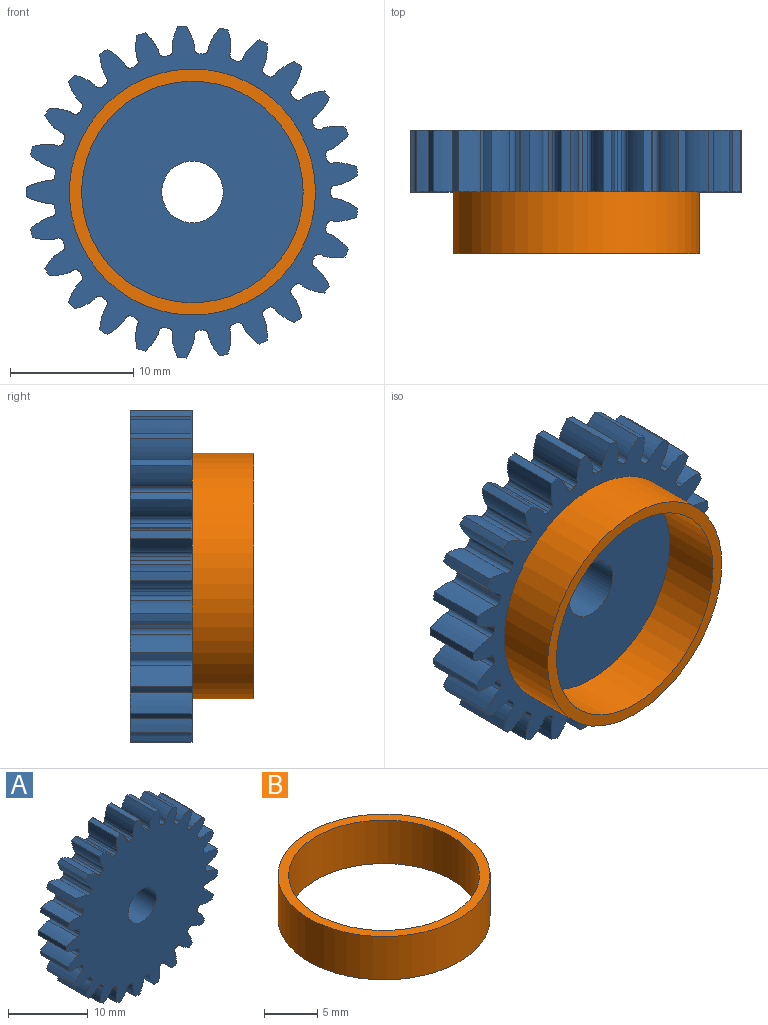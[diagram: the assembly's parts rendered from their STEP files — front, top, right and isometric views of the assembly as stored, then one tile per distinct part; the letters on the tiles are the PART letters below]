
ASSEMBLY  parts=2 mates=1
PART A: 153 faces, bbox 26.9x5x27 mm
  f0: cylinder r=13.5mm len=5mm, axis (0,1,0), area 3.6mm2, adj f24,f27,f138,f150
  f1: cylinder r=13.5mm len=5mm, axis (0,1,0), area 3.6mm2, adj f24,f27,f145,f148
  f2: cylinder r=13.5mm len=5mm, axis (0,1,0), area 3.6mm2, adj f24,f27,f133,f140
  f3: cylinder r=13.5mm len=5mm, axis (0,1,0), area 3.6mm2, adj f24,f27,f128,f135
  f4: cylinder r=13.5mm len=5mm, axis (0,1,0), area 3.6mm2, adj f24,f27,f123,f130
  f5: cylinder r=13.5mm len=5mm, axis (0,1,0), area 3.6mm2, adj f24,f27,f113,f125
  f6: cylinder r=13.5mm len=5mm, axis (0,1,0), area 3.6mm2, adj f24,f27,f108,f120
  f7: cylinder r=13.5mm len=5mm, axis (0,1,0), area 3.6mm2, adj f24,f27,f115,f118
  f8: cylinder r=13.5mm len=5mm, axis (0,1,0), area 3.6mm2, adj f24,f27,f103,f110
  f9: cylinder r=13.5mm len=5mm, axis (0,1,0), area 3.6mm2, adj f24,f27,f98,f105
  f10: cylinder r=13.5mm len=5mm, axis (0,1,0), area 3.6mm2, adj f24,f27,f93,f100
  f11: cylinder r=13.5mm len=5mm, axis (0,1,0), area 3.6mm2, adj f24,f27,f78,f95
  f12: cylinder r=13.5mm len=5mm, axis (0,1,0), area 3.6mm2, adj f24,f27,f28,f90
  f13: cylinder r=13.5mm len=5mm, axis (0,1,0), area 3.6mm2, adj f24,f27,f85,f88
  f14: cylinder r=13.5mm len=5mm, axis (0,1,0), area 3.6mm2, adj f24,f27,f73,f80
  f15: cylinder r=13.5mm len=5mm, axis (0,1,0), area 3.6mm2, adj f24,f27,f75,f83
  f16: cylinder r=13.5mm len=5mm, axis (0,1,0), area 3.6mm2, adj f24,f27,f70,f143
  f17: cylinder r=13.5mm len=5mm, axis (0,1,0), area 3.6mm2, adj f24,f27,f65,f68
  f18: cylinder r=13.5mm len=5mm, axis (0,1,0), area 3.6mm2, adj f24,f27,f60,f63
  f19: cylinder r=13.5mm len=5mm, axis (0,1,0), area 3.6mm2, adj f24,f27,f55,f58
  f20: cylinder r=13.5mm len=5mm, axis (0,1,0), area 3.6mm2, adj f24,f27,f43,f50
  f21: cylinder r=13.5mm len=5mm, axis (0,1,0), area 3.6mm2, adj f24,f27,f33,f45
  f22: cylinder r=13.5mm len=5mm, axis (0,1,0), area 3.6mm2, adj f24,f27,f40,f53
  f23: cylinder r=13.5mm len=5mm, axis (0,1,0), area 3.6mm2, adj f24,f27,f35,f38
  f24: plane 26.99x26.94mm, normal (0,-1,0), area 464mm2, adj f0,f1,f2,f3,f4,f5,f6,f7
  f25: cylinder r=2.5mm len=5mm, axis (0,1,0), area 78.5mm2, adj f24,f27
  f26: cylinder r=13.5mm len=5mm, axis (0,1,0), area 3.6mm2, adj f24,f27,f30,f48
  f27: plane 26.99x26.94mm, normal (0,1,0), area 464mm2, adj f0,f1,f2,f3,f4,f5,f6,f7
  f28: extruded ~5x1.83mm, area 10mm2, adj f12,f24,f27,f31
  f29: cylinder r=11.25mm len=5mm, axis (0,1,0), area 1.7mm2, adj f24,f27,f31,f32
  f30: extruded ~5x1.83mm, area 10mm2, adj f24,f26,f27,f32
  f31: cylinder r=0.38mm len=5mm, axis (0,1,0), area 2.9mm2, adj f24,f27,f28,f29
  f32: cylinder r=0.38mm len=5mm, axis (0,1,0), area 2.9mm2, adj f24,f27,f29,f30
  f33: extruded ~5x1.86mm, area 10mm2, adj f21,f24,f27,f36
  f34: cylinder r=11.25mm len=5mm, axis (0,1,0), area 1.7mm2, adj f24,f27,f36,f37
  f35: extruded ~5x1.82mm, area 10mm2, adj f23,f24,f27,f37
  f36: cylinder r=0.38mm len=5mm, axis (0,1,0), area 2.9mm2, adj f24,f27,f33,f34
  f37: cylinder r=0.38mm len=5mm, axis (0,1,0), area 2.9mm2, adj f24,f27,f34,f35
  f38: extruded ~5x1.64mm, area 10mm2, adj f23,f24,f27,f41
  f39: cylinder r=11.25mm len=5mm, axis (0,1,0), area 1.7mm2, adj f24,f27,f41,f42
  f40: extruded ~5x1.96mm, area 10mm2, adj f22,f24,f27,f42
  f41: cylinder r=0.38mm len=5mm, axis (0,1,0), area 2.9mm2, adj f24,f27,f38,f39
  f42: cylinder r=0.38mm len=5mm, axis (0,1,0), area 2.9mm2, adj f24,f27,f39,f40
  f43: extruded ~5x1.98mm, area 10mm2, adj f20,f24,f27,f46
  f44: cylinder r=11.25mm len=5mm, axis (0,1,0), area 1.7mm2, adj f24,f27,f46,f47
  f45: extruded ~5x1.56mm, area 10mm2, adj f21,f24,f27,f47
  f46: cylinder r=0.38mm len=5mm, axis (0,1,0), area 2.9mm2, adj f24,f27,f43,f44
  f47: cylinder r=0.38mm len=5mm, axis (0,1,0), area 2.9mm2, adj f24,f27,f44,f45
  f48: extruded ~5x1.96mm, area 10mm2, adj f24,f26,f27,f51
  f49: cylinder r=11.25mm len=5mm, axis (0,1,0), area 1.7mm2, adj f24,f27,f51,f52
  f50: extruded ~5x1.57mm, area 10mm2, adj f20,f24,f27,f52
  f51: cylinder r=0.38mm len=5mm, axis (0,1,0), area 2.9mm2, adj f24,f27,f48,f49
  f52: cylinder r=0.38mm len=5mm, axis (0,1,0), area 2.9mm2, adj f24,f27,f49,f50
  f53: extruded ~5x1.5mm, area 10mm2, adj f22,f24,f27,f56
  f54: cylinder r=11.25mm len=5mm, axis (0,1,0), area 1.7mm2, adj f24,f27,f56,f57
  f55: extruded ~5x1.98mm, area 10mm2, adj f19,f24,f27,f57
  f56: cylinder r=0.38mm len=5mm, axis (0,1,0), area 2.9mm2, adj f24,f27,f53,f54
  f57: cylinder r=0.38mm len=5mm, axis (0,1,0), area 2.9mm2, adj f24,f27,f54,f55
  f58: extruded ~5x1.77mm, area 10mm2, adj f19,f24,f27,f61
  f59: cylinder r=11.25mm len=5mm, axis (0,1,0), area 1.7mm2, adj f24,f27,f61,f62
  f60: extruded ~5x1.87mm, area 10mm2, adj f18,f24,f27,f62
  f61: cylinder r=0.38mm len=5mm, axis (0,1,0), area 2.9mm2, adj f24,f27,f58,f59
  f62: cylinder r=0.38mm len=5mm, axis (0,1,0), area 2.9mm2, adj f24,f27,f59,f60
  f63: extruded ~5x1.94mm, area 10mm2, adj f18,f24,f27,f66
  f64: cylinder r=11.25mm len=5mm, axis (0,1,0), area 1.7mm2, adj f24,f27,f66,f67
  f65: extruded ~5x1.65mm, area 10mm2, adj f17,f24,f27,f67
  f66: cylinder r=0.38mm len=5mm, axis (0,1,0), area 2.9mm2, adj f24,f27,f63,f64
  f67: cylinder r=0.38mm len=5mm, axis (0,1,0), area 2.9mm2, adj f24,f27,f64,f65
  f68: extruded ~5x1.98mm, area 10mm2, adj f17,f24,f27,f71
  f69: cylinder r=11.25mm len=5mm, axis (0,1,0), area 1.7mm2, adj f24,f27,f71,f72
  f70: extruded ~5x1.48mm, area 10mm2, adj f16,f24,f27,f72
  f71: cylinder r=0.38mm len=5mm, axis (0,1,0), area 2.9mm2, adj f24,f27,f68,f69
  f72: cylinder r=0.38mm len=5mm, axis (0,1,0), area 2.9mm2, adj f24,f27,f69,f70
  f73: extruded ~5x1.82mm, area 10mm2, adj f14,f24,f27,f76
  f74: cylinder r=11.25mm len=5mm, axis (0,1,0), area 1.7mm2, adj f24,f27,f76,f77
  f75: extruded ~5x1.86mm, area 10mm2, adj f15,f24,f27,f77
  f76: cylinder r=0.38mm len=5mm, axis (0,1,0), area 2.9mm2, adj f24,f27,f73,f74
  f77: cylinder r=0.38mm len=5mm, axis (0,1,0), area 2.9mm2, adj f24,f27,f74,f75
  f78: extruded ~5x1.96mm, area 10mm2, adj f11,f24,f27,f81
  f79: cylinder r=11.25mm len=5mm, axis (0,1,0), area 1.7mm2, adj f24,f27,f81,f82
  f80: extruded ~5x1.64mm, area 10mm2, adj f14,f24,f27,f82
  f81: cylinder r=0.38mm len=5mm, axis (0,1,0), area 2.9mm2, adj f24,f27,f78,f79
  f82: cylinder r=0.38mm len=5mm, axis (0,1,0), area 2.9mm2, adj f24,f27,f79,f80
  f83: extruded ~5x1.56mm, area 10mm2, adj f15,f24,f27,f86
  f84: cylinder r=11.25mm len=5mm, axis (0,1,0), area 1.7mm2, adj f24,f27,f86,f87
  f85: extruded ~5x1.98mm, area 10mm2, adj f13,f24,f27,f87
  f86: cylinder r=0.38mm len=5mm, axis (0,1,0), area 2.9mm2, adj f24,f27,f83,f84
  f87: cylinder r=0.38mm len=5mm, axis (0,1,0), area 2.9mm2, adj f24,f27,f84,f85
  f88: extruded ~5x1.57mm, area 10mm2, adj f13,f24,f27,f91
  f89: cylinder r=11.25mm len=5mm, axis (0,1,0), area 1.7mm2, adj f24,f27,f91,f92
  f90: extruded ~5x1.96mm, area 10mm2, adj f12,f24,f27,f92
  f91: cylinder r=0.38mm len=5mm, axis (0,1,0), area 2.9mm2, adj f24,f27,f88,f89
  f92: cylinder r=0.38mm len=5mm, axis (0,1,0), area 2.9mm2, adj f24,f27,f89,f90
  f93: extruded ~5x1.98mm, area 10mm2, adj f10,f24,f27,f96
  f94: cylinder r=11.25mm len=5mm, axis (0,1,0), area 1.7mm2, adj f24,f27,f96,f97
  f95: extruded ~5x1.5mm, area 10mm2, adj f11,f24,f27,f97
  f96: cylinder r=0.38mm len=5mm, axis (0,1,0), area 2.9mm2, adj f24,f27,f93,f94
  f97: cylinder r=0.38mm len=5mm, axis (0,1,0), area 2.9mm2, adj f24,f27,f94,f95
  f98: extruded ~5x1.87mm, area 10mm2, adj f9,f24,f27,f101
  f99: cylinder r=11.25mm len=5mm, axis (0,1,0), area 1.7mm2, adj f24,f27,f101,f102
  f100: extruded ~5x1.77mm, area 10mm2, adj f10,f24,f27,f102
  f101: cylinder r=0.38mm len=5mm, axis (0,1,0), area 2.9mm2, adj f24,f27,f98,f99
  f102: cylinder r=0.38mm len=5mm, axis (0,1,0), area 2.9mm2, adj f24,f27,f99,f100
  f103: extruded ~5x1.65mm, area 10mm2, adj f8,f24,f27,f106
  f104: cylinder r=11.25mm len=5mm, axis (0,1,0), area 1.7mm2, adj f24,f27,f106,f107
  f105: extruded ~5x1.94mm, area 10mm2, adj f9,f24,f27,f107
  f106: cylinder r=0.38mm len=5mm, axis (0,1,0), area 2.9mm2, adj f24,f27,f103,f104
  f107: cylinder r=0.38mm len=5mm, axis (0,1,0), area 2.9mm2, adj f24,f27,f104,f105
  f108: extruded ~5x1.48mm, area 10mm2, adj f6,f24,f27,f111
  f109: cylinder r=11.25mm len=5mm, axis (0,1,0), area 1.7mm2, adj f24,f27,f111,f112
  f110: extruded ~5x1.98mm, area 10mm2, adj f8,f24,f27,f112
  f111: cylinder r=0.38mm len=5mm, axis (0,1,0), area 2.9mm2, adj f24,f27,f108,f109
  f112: cylinder r=0.38mm len=5mm, axis (0,1,0), area 2.9mm2, adj f24,f27,f109,f110
  f113: extruded ~5x1.93mm, area 10mm2, adj f5,f24,f27,f116
  f114: cylinder r=11.25mm len=5mm, axis (0,1,0), area 1.7mm2, adj f24,f27,f116,f117
  f115: extruded ~5x1.7mm, area 10mm2, adj f7,f24,f27,f117
  f116: cylinder r=0.38mm len=5mm, axis (0,1,0), area 2.9mm2, adj f24,f27,f113,f114
  f117: cylinder r=0.38mm len=5mm, axis (0,1,0), area 2.9mm2, adj f24,f27,f114,f115
  f118: extruded ~5x1.76mm, area 10mm2, adj f7,f24,f27,f121
  f119: cylinder r=11.25mm len=5mm, axis (0,1,0), area 1.7mm2, adj f24,f27,f121,f122
  f120: extruded ~5x1.9mm, area 10mm2, adj f6,f24,f27,f122
  f121: cylinder r=0.38mm len=5mm, axis (0,1,0), area 2.9mm2, adj f24,f27,f118,f119
  f122: cylinder r=0.38mm len=5mm, axis (0,1,0), area 2.9mm2, adj f24,f27,f119,f120
  f123: extruded ~5x1.98mm, area 10mm2, adj f4,f24,f27,f126
  f124: cylinder r=11.25mm len=5mm, axis (0,1,0), area 1.7mm2, adj f24,f27,f126,f127
  f125: extruded ~5x1.41mm, area 10mm2, adj f5,f24,f27,f127
  f126: cylinder r=0.38mm len=5mm, axis (0,1,0), area 2.9mm2, adj f24,f27,f123,f124
  f127: cylinder r=0.38mm len=5mm, axis (0,1,0), area 2.9mm2, adj f24,f27,f124,f125
  f128: extruded ~5x1.91mm, area 10mm2, adj f3,f24,f27,f131
  f129: cylinder r=11.25mm len=5mm, axis (0,1,0), area 1.7mm2, adj f24,f27,f131,f132
  f130: extruded ~5x1.71mm, area 10mm2, adj f4,f24,f27,f132
  f131: cylinder r=0.38mm len=5mm, axis (0,1,0), area 2.9mm2, adj f24,f27,f128,f129
  f132: cylinder r=0.38mm len=5mm, axis (0,1,0), area 2.9mm2, adj f24,f27,f129,f130
  f133: extruded ~5x1.71mm, area 10mm2, adj f2,f24,f27,f136
  f134: cylinder r=11.25mm len=5mm, axis (0,1,0), area 1.7mm2, adj f24,f27,f136,f137
  f135: extruded ~5x1.91mm, area 10mm2, adj f3,f24,f27,f137
  f136: cylinder r=0.38mm len=5mm, axis (0,1,0), area 2.9mm2, adj f24,f27,f133,f134
  f137: cylinder r=0.38mm len=5mm, axis (0,1,0), area 2.9mm2, adj f24,f27,f134,f135
  f138: extruded ~5x1.41mm, area 10mm2, adj f0,f24,f27,f141
  f139: cylinder r=11.25mm len=5mm, axis (0,1,0), area 1.7mm2, adj f24,f27,f141,f142
  f140: extruded ~5x1.98mm, area 10mm2, adj f2,f24,f27,f142
  f141: cylinder r=0.38mm len=5mm, axis (0,1,0), area 2.9mm2, adj f24,f27,f138,f139
  f142: cylinder r=0.38mm len=5mm, axis (0,1,0), area 2.9mm2, adj f24,f27,f139,f140
  f143: extruded ~5x1.9mm, area 10mm2, adj f16,f24,f27,f146
  f144: cylinder r=11.25mm len=5mm, axis (0,1,0), area 1.7mm2, adj f24,f27,f146,f147
  f145: extruded ~5x1.76mm, area 10mm2, adj f1,f24,f27,f147
  f146: cylinder r=0.38mm len=5mm, axis (0,1,0), area 2.9mm2, adj f24,f27,f143,f144
  f147: cylinder r=0.38mm len=5mm, axis (0,1,0), area 2.9mm2, adj f24,f27,f144,f145
  f148: extruded ~5x1.7mm, area 10mm2, adj f1,f24,f27,f151
  f149: cylinder r=11.25mm len=5mm, axis (0,1,0), area 1.7mm2, adj f24,f27,f151,f152
  f150: extruded ~5x1.93mm, area 10mm2, adj f0,f24,f27,f152
  f151: cylinder r=0.38mm len=5mm, axis (0,1,0), area 2.9mm2, adj f24,f27,f148,f149
  f152: cylinder r=0.38mm len=5mm, axis (0,1,0), area 2.9mm2, adj f24,f27,f149,f150
PART B: 4 faces, bbox 20x20x5 mm
  f0: cylinder r=9mm len=18mm, axis (0,0,-1), area 282.7mm2, adj f2,f3
  f1: cylinder r=10mm len=20mm, axis (0,0,-1), area 314.2mm2, adj f2,f3
  f2: plane 20x20mm, normal (0,0,1), area 59.7mm2, adj f0,f1
  f3: plane 20x20mm, normal (0,0,-1), area 59.7mm2, adj f0,f1
PLACE A at identity fixed
PLACE B rot(axis=(1,0,0),90deg) t=(0,-5,0)mm
MATE fastened A.f0 <-> B.f1  axis (0,-1,0) through (0,-5,0)mm
